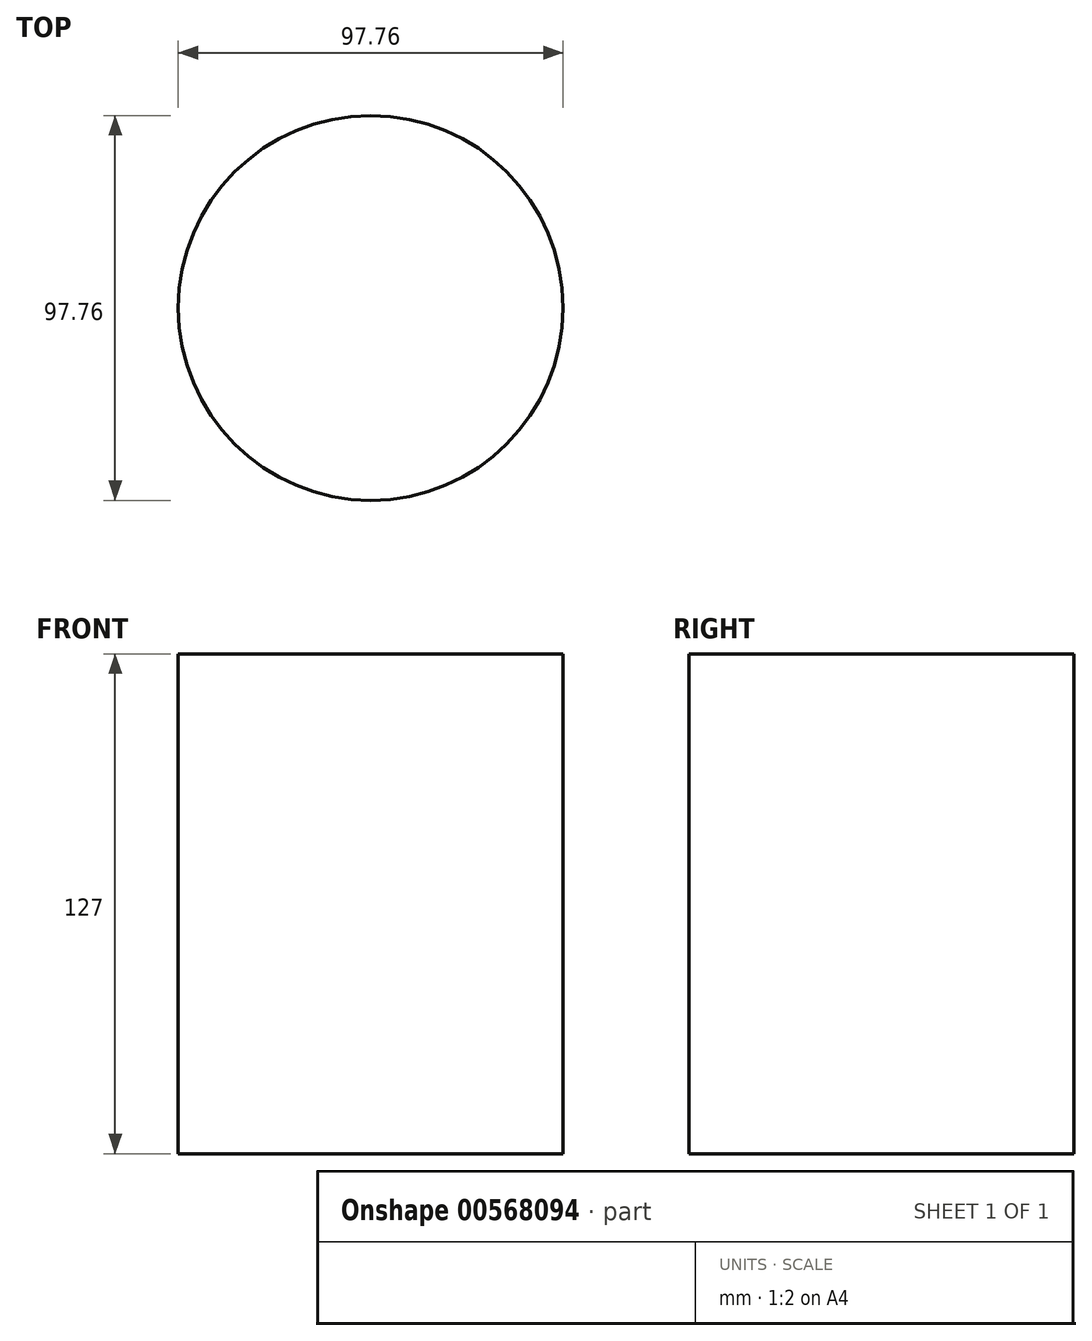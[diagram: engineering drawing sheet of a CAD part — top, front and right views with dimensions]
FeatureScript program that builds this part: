
annotation { "Feature Type Name" : "Feature", "Feature Type Description" : "" }
export const myFeature = defineFeature(function(context is Context, id is Id, definition is map)
    precondition{}
    {
        {
            var Q0;
            Q0=qCreatedBy(makeId("Top.planeOp"),FACE);
            var sketch = newSketch(context, id + "F0", { "sketchPlane" : qUnion([Q0])});
            skCircle(sketch, "E0", {"center": v(0, 0) * mm, "radius": 42.53 * mm});
            skCircle(sketch, "E1.0", {"center": v(0, 0) * mm, "radius": 48.88 * mm});
            skSolve(sketch);
        }
        {
            var Q0;
            Q0=sQuery(id+"F0.wireOp",EDGE,"E1.0");
            extrude(context, id + "F1", {"bodyType" : ToolBodyType.SURFACE, "surfaceEntities" : qUnion([Q0]), "depth" : 127 * mm, "offsetDistance" : 25.4 * mm});
        }
    });
